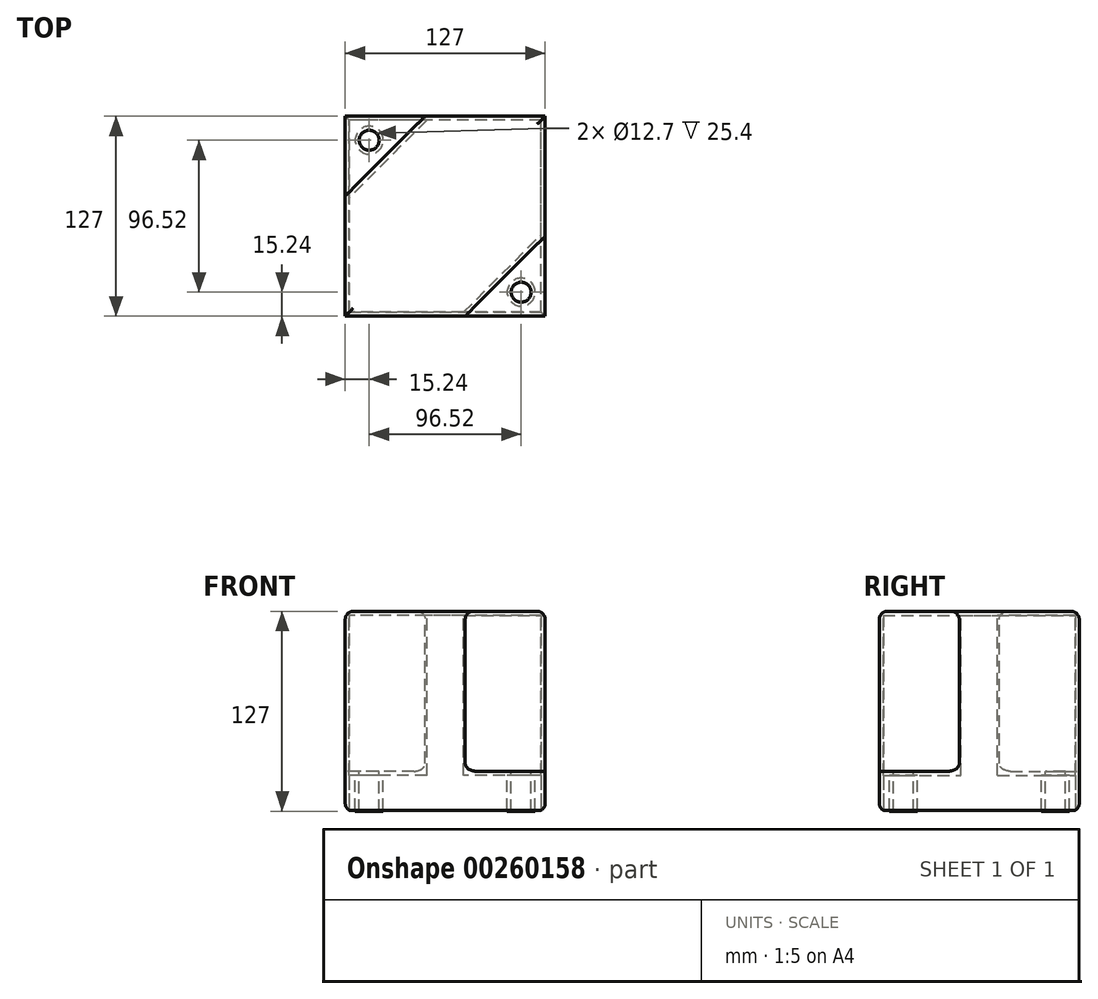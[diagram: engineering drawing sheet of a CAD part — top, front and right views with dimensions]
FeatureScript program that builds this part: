
annotation { "Feature Type Name" : "Feature", "Feature Type Description" : "" }
export const myFeature = defineFeature(function(context is Context, id is Id, definition is map)
    precondition{}
    {
        {
            var Q0;
            Q0=qCreatedBy(makeId("Top.planeOp"),FACE);
            var sketch = newSketch(context, id + "F0", { "sketchPlane" : qUnion([Q0])});
            skLineSegment(sketch, "E0.bottom", {"start": v(63.5, -63.5) * mm, "end": v(-63.5, -63.5) * mm});
            skLineSegment(sketch, "E0.top", {"start": v(63.5, 63.5) * mm, "end": v(-63.5, 63.5) * mm});
            skLineSegment(sketch, "E0.left", {"start": v(63.5, -63.5) * mm, "end": v(63.5, 63.5) * mm});
            skLineSegment(sketch, "E0.right", {"start": v(-63.5, -63.5) * mm, "end": v(-63.5, 63.5) * mm});
            skPoint(sketch, "E0.middle", {"position": v(0, 0) * mm});
            skSolve(sketch);
        }
        {
            var Q0;
            Q0=makeQuery(id+"F0.imprint","IMPRINT",FACE,{"disambiguationData":[TD([[makeQuery(id+"F0.imprint","IMPRINT",EDGE,{"derivedFrom":sQuery(id+"F0.wireOp",EDGE,"E0.bottom")}),-1.0]])]});
            extrude(context, id + "F1", {"entities" : qUnion([Q0]), "depth" : 127 * mm});
        }
        {
            var Q0;
            Q0=makeQuery(id+"F1.opExtrude","CAP_FACE",FACE,{"disambiguationData":[OSD([sQuery(id+"F0.wireOp",EDGE,"E0.bottom"),sQuery(id+"F0.wireOp",EDGE,"E0.top"),sQuery(id+"F0.wireOp",EDGE,"E0.left"),sQuery(id+"F0.wireOp",EDGE,"E0.right")])],"isStart":false});
            var sketch = newSketch(context, id + "F2", { "sketchPlane" : qUnion([Q0])});
            skLineSegment(sketch, "E1", {"start": v(-63.5, 63.5) * mm, "end": v(-63.5, 12.7) * mm});
            skLineSegment(sketch, "E2", {"start": v(-63.5, 63.5) * mm, "end": v(-12.7, 63.5) * mm});
            skLineSegment(sketch, "E3", {"start": v(-12.7, 63.5) * mm, "end": v(-63.5, 12.7) * mm});
            skLineSegment(sketch, "E4", {"start": v(63.5, -63.5) * mm, "end": v(63.5, -12.7) * mm});
            skLineSegment(sketch, "E5", {"start": v(63.5, -63.5) * mm, "end": v(12.7, -63.5) * mm});
            skLineSegment(sketch, "E6", {"start": v(12.7, -63.5) * mm, "end": v(63.5, -12.7) * mm});
            skSolve(sketch);
        }
        {
            var Q0;
            Q0=makeQuery(id+"F2.imprint","IMPRINT",FACE,{"disambiguationData":[TD([[makeQuery(id+"F2.imprint","IMPRINT",EDGE,{"derivedFrom":sQuery(id+"F2.wireOp",EDGE,"E4")}),1.0]])]});
            var Q1;
            Q1=makeQuery(id+"F2.imprint","IMPRINT",FACE,{"disambiguationData":[TD([[makeQuery(id+"F2.imprint","IMPRINT",EDGE,{"derivedFrom":sQuery(id+"F2.wireOp",EDGE,"E1")}),-1.0]])]});
            extrude(context, id + "F3", {"entities" : qUnion([Q0, Q1]), "operationType" : NewBodyOperationType.REMOVE, "oppositeDirection" : true, "depth" : 101.6 * mm});
        }
        {
            var Q0;
            Q0=makeQuery(id+"F3.boolean.opBoolean","COPY",FACE,{"derivedFrom":makeQuery(id+"F3.opExtrude","CAP_FACE",FACE,{"disambiguationData":[OSD([sQuery(id+"F2.wireOp",EDGE,"E4"),sQuery(id+"F2.wireOp",EDGE,"E5"),sQuery(id+"F2.wireOp",EDGE,"E6")])],"isStart":false})});
            var sketch = newSketch(context, id + "F4", { "sketchPlane" : qUnion([Q0])});
            skCircle(sketch, "E7", {"center": v(48.26, -48.26) * mm, "radius": 6.35 * mm});
            skCircle(sketch, "E8", {"center": v(-48.26, 48.26) * mm, "radius": 6.35 * mm});
            skSolve(sketch);
        }
        {
            var Q0;
            Q0=makeQuery(id+"F4.imprint","IMPRINT",FACE,{"disambiguationData":[TD([[makeQuery(id+"F4.imprint","IMPRINT",EDGE,{"derivedFrom":sQuery(id+"F4.wireOp",EDGE,"E8")}),1.0]])]});
            var Q1;
            Q1=makeQuery(id+"F4.imprint","IMPRINT",FACE,{"disambiguationData":[TD([[makeQuery(id+"F4.imprint","IMPRINT",EDGE,{"derivedFrom":sQuery(id+"F4.wireOp",EDGE,"E7")}),1.0]])]});
            var Q2;
            Q2=sQuery(id+"F4.wireOp",EDGE,"E8");
            var Q3;
            Q3=sQuery(id+"F4.wireOp",EDGE,"E7");
            extrude(context, id + "F5", {"entities" : qUnion([Q0, Q1]), "operationType" : NewBodyOperationType.REMOVE, "surfaceEntities" : qUnion([Q2, Q3]), "oppositeDirection" : true, "depth" : 203.2 * mm});
        }
        {
            var Q0;
            Q0=makeQuery(id+"F1.opExtrude","CAP_FACE",FACE,{"disambiguationData":[OSD([sQuery(id+"F0.wireOp",EDGE,"E0.bottom"),sQuery(id+"F0.wireOp",EDGE,"E0.top"),sQuery(id+"F0.wireOp",EDGE,"E0.left"),sQuery(id+"F0.wireOp",EDGE,"E0.right")])],"isStart":true});
            shell(context, id + "F6", {"entities" : qUnion([Q0]), "thickness" : 2.54 * mm});
        }
        {
            var Q0;
            Q0=makeQuery(id+"F1.opExtrude","CAP_EDGE",EDGE,{"disambiguationData":[OSD([sQuery(id+"F0.wireOp",EDGE,"E0.bottom")])],"isStart":false});
            var Q1;
            Q1=makeQuery(id+"F3.boolean.opBoolean","COPY",EDGE,{"derivedFrom":makeQuery(id+"F3.opExtrude","CAP_EDGE",EDGE,{"disambiguationData":[OSD([sQuery(id+"F2.wireOp",EDGE,"E6")])],"isStart":true})});
            var Q2;
            Q2=makeQuery(id+"F1.opExtrude","CAP_EDGE",EDGE,{"disambiguationData":[OSD([sQuery(id+"F0.wireOp",EDGE,"E0.left")])],"isStart":false});
            var Q3;
            Q3=makeQuery(id+"F1.opExtrude","CAP_EDGE",EDGE,{"disambiguationData":[OSD([sQuery(id+"F0.wireOp",EDGE,"E0.top")])],"isStart":false});
            var Q4;
            Q4=makeQuery(id+"F3.boolean.opBoolean","COPY",EDGE,{"derivedFrom":makeQuery(id+"F3.opExtrude","CAP_EDGE",EDGE,{"disambiguationData":[OSD([sQuery(id+"F2.wireOp",EDGE,"E3")])],"isStart":true})});
            var Q5;
            Q5=makeQuery(id+"F1.opExtrude","CAP_EDGE",EDGE,{"disambiguationData":[OSD([sQuery(id+"F0.wireOp",EDGE,"E0.right")])],"isStart":false});
            var Q6;
            Q6=makeQuery(id+"F3.boolean.opBoolean","COPY",EDGE,{"derivedFrom":makeQuery(id+"F3.opExtrude","SWEPT_EDGE",EDGE,{"disambiguationData":[OSD([sQuery(id+"F0.wireOp",EDGE,"E0.right"),sQuery(id+"F2.wireOp",EDGE,"E1"),sQuery(id+"F2.wireOp",EDGE,"E3")])]})});
            var Q7;
            Q7=makeQuery(id+"F3.boolean.opBoolean","COPY",EDGE,{"derivedFrom":makeQuery(id+"F3.opExtrude","SWEPT_EDGE",EDGE,{"disambiguationData":[OSD([sQuery(id+"F0.wireOp",EDGE,"E0.top"),sQuery(id+"F2.wireOp",EDGE,"E2"),sQuery(id+"F2.wireOp",EDGE,"E3")])]})});
            var Q8;
            Q8=makeQuery(id+"F3.boolean.opBoolean","COPY",EDGE,{"derivedFrom":makeQuery(id+"F3.opExtrude","SWEPT_EDGE",EDGE,{"disambiguationData":[OSD([sQuery(id+"F0.wireOp",EDGE,"E0.left"),sQuery(id+"F2.wireOp",EDGE,"E4"),sQuery(id+"F2.wireOp",EDGE,"E6")])]})});
            var Q9;
            Q9=makeQuery(id+"F3.boolean.opBoolean","COPY",EDGE,{"derivedFrom":makeQuery(id+"F3.opExtrude","SWEPT_EDGE",EDGE,{"disambiguationData":[OSD([sQuery(id+"F0.wireOp",EDGE,"E0.bottom"),sQuery(id+"F2.wireOp",EDGE,"E5"),sQuery(id+"F2.wireOp",EDGE,"E6")])]})});
            var Q10;
            Q10=makeQuery(id+"F3.boolean.opBoolean","COPY",EDGE,{"derivedFrom":makeQuery(id+"F3.opExtrude","CAP_EDGE",EDGE,{"disambiguationData":[OSD([sQuery(id+"F2.wireOp",EDGE,"E5")])],"isStart":false})});
            var Q11;
            Q11=makeQuery(id+"F3.boolean.opBoolean","COPY",EDGE,{"derivedFrom":makeQuery(id+"F3.opExtrude","CAP_EDGE",EDGE,{"disambiguationData":[OSD([sQuery(id+"F2.wireOp",EDGE,"E4")])],"isStart":false})});
            var Q12;
            Q12=makeQuery(id+"F3.boolean.opBoolean","COPY",EDGE,{"derivedFrom":makeQuery(id+"F3.opExtrude","CAP_EDGE",EDGE,{"disambiguationData":[OSD([sQuery(id+"F2.wireOp",EDGE,"E6")])],"isStart":false})});
            var Q13;
            Q13=makeQuery(id+"F3.boolean.opBoolean","COPY",EDGE,{"derivedFrom":makeQuery(id+"F3.opExtrude","CAP_EDGE",EDGE,{"disambiguationData":[OSD([sQuery(id+"F2.wireOp",EDGE,"E2")])],"isStart":false})});
            var Q14;
            Q14=makeQuery(id+"F3.boolean.opBoolean","COPY",EDGE,{"derivedFrom":makeQuery(id+"F3.opExtrude","CAP_EDGE",EDGE,{"disambiguationData":[OSD([sQuery(id+"F2.wireOp",EDGE,"E3")])],"isStart":false})});
            var Q15;
            Q15=makeQuery(id+"F3.boolean.opBoolean","COPY",EDGE,{"derivedFrom":makeQuery(id+"F3.opExtrude","CAP_EDGE",EDGE,{"disambiguationData":[OSD([sQuery(id+"F2.wireOp",EDGE,"E1")])],"isStart":false})});
            var Q16;
            Q16=makeQuery(id+"F1.opExtrude","CAP_EDGE",EDGE,{"disambiguationData":[OSD([sQuery(id+"F0.wireOp",EDGE,"E0.bottom")])],"isStart":true});
            var Q17;
            Q17=makeQuery(id+"F1.opExtrude","CAP_EDGE",EDGE,{"disambiguationData":[OSD([sQuery(id+"F0.wireOp",EDGE,"E0.top")])],"isStart":true});
            var Q18;
            Q18=makeQuery(id+"F1.opExtrude","CAP_EDGE",EDGE,{"disambiguationData":[OSD([sQuery(id+"F0.wireOp",EDGE,"E0.right")])],"isStart":true});
            var Q19;
            Q19=makeQuery(id+"F1.opExtrude","CAP_EDGE",EDGE,{"disambiguationData":[OSD([sQuery(id+"F0.wireOp",EDGE,"E0.left")])],"isStart":true});
            fillet(context, id + "F7", {"entities" : qUnion([Q0, Q1, Q2, Q3, Q4, Q5, Q6, Q7, Q8, Q9, Q10, Q11, Q12, Q13, Q14, Q15, Q16, Q17, Q18, Q19]), "radius" : 5.08 * mm, "tangentPropagation" : true, "allowEdgeOverflow" : false});
        }
    });
